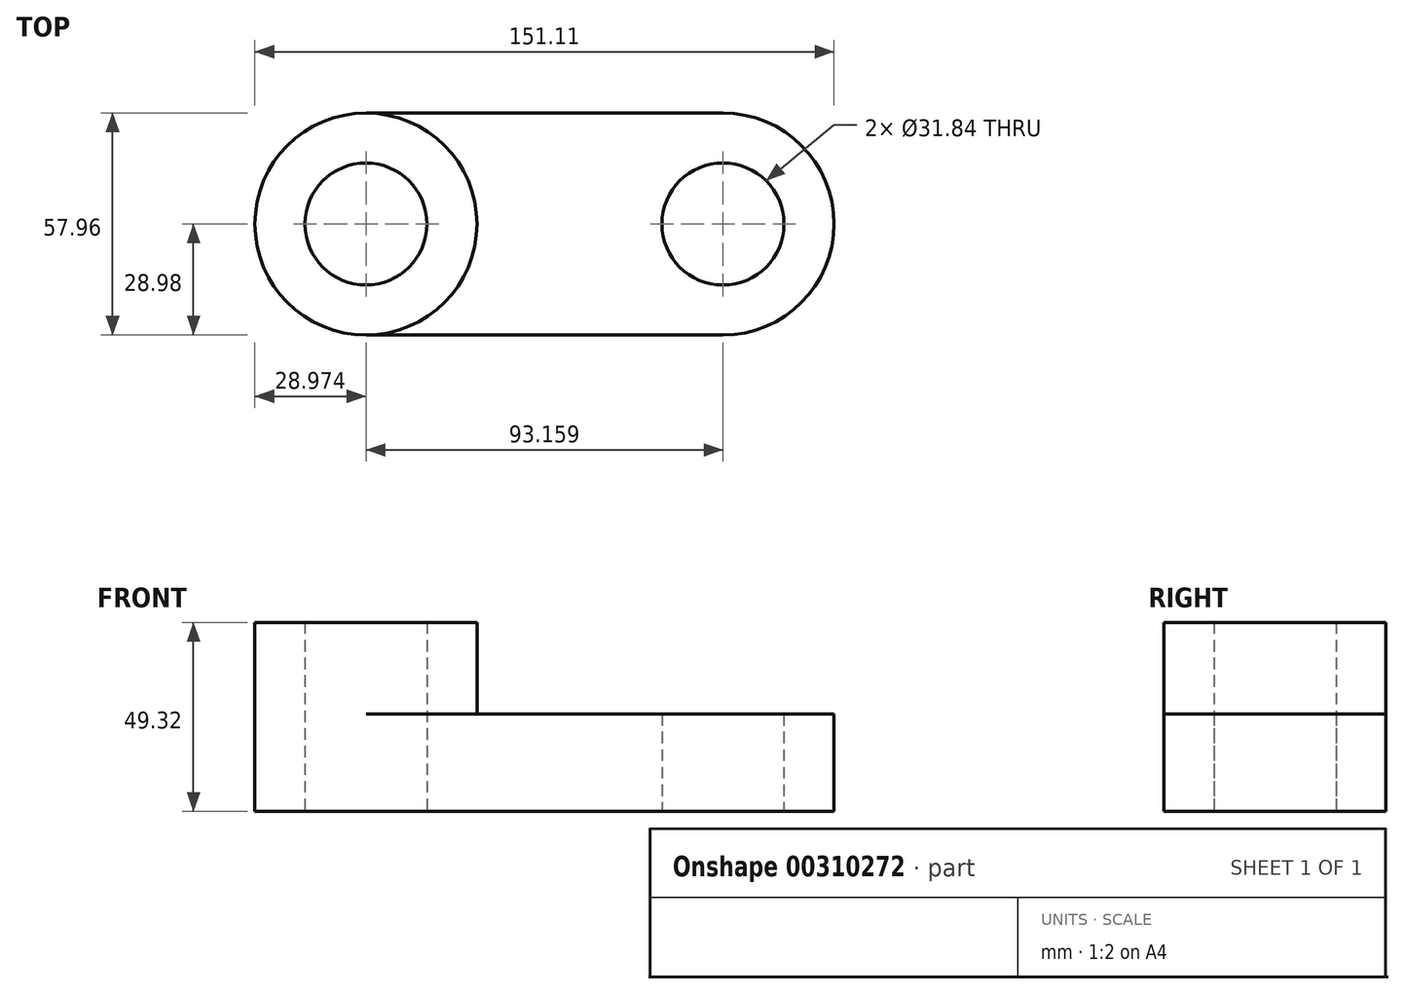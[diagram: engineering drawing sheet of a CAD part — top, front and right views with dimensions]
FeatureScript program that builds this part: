
annotation { "Feature Type Name" : "Feature", "Feature Type Description" : "" }
export const myFeature = defineFeature(function(context is Context, id is Id, definition is map)
    precondition{}
    {
        {
            var Q0;
            Q0=qCreatedBy(makeId("Top.planeOp"),FACE);
            var sketch = newSketch(context, id + "F0", { "sketchPlane" : qUnion([Q0])});
            skLineSegment(sketch, "E0", {"start": v(-142.42, 0) * mm, "end": v(-142.42, 0) * mm});
            skPoint(sketch, "E0.endSnap0", {"position": v(59.82, 0) * mm});
            skLineSegment(sketch, "E1", {"start": v(-49.26, 46.21) * mm, "end": v(-49.26, -63.45) * mm, "construction": true});
            skLineSegment(sketch, "E2", {"start": v(43.9, 44.72) * mm, "end": v(43.9, -62.7) * mm, "construction": true});
            skArc(sketch, "E3", {"start": v(43.9, -28.98) * mm, "mid": v(72.88, 0) * mm, "end": v(43.9, 28.98) * mm});
            skLineSegment(sketch, "E4", {"start": v(-49.26, 28.98) * mm, "end": v(43.9, 28.98) * mm});
            skLineSegment(sketch, "E5", {"start": v(-49.26, -28.98) * mm, "end": v(43.9, -28.98) * mm});
            skPoint(sketch, "E6.orphan", {"position": v(43.9, 15.92) * mm});
            skCircle(sketch, "E7", {"center": v(-49.26, 0) * mm, "radius": 15.92 * mm});
            skCircle(sketch, "E8", {"center": v(43.9, 0) * mm, "radius": 15.92 * mm});
            skLineSegment(sketch, "E9", {"start": v(-96.05, 0) * mm, "end": v(92.92, 0) * mm, "construction": true});
            skPoint(sketch, "E9.endSnap0", {"position": v(72.88, 0) * mm});
            skCircle(sketch, "E10.converted", {"center": v(-49.26, 0) * mm, "radius": 28.98 * mm});
            skSolve(sketch);
        }
        {
            var Q0;
            Q0=makeQuery(id+"F0.imprint","IMPRINT",FACE,{"disambiguationData":[TD([[makeQuery(id+"F0.imprint","IMPRINT",EDGE,{"derivedFrom":sQuery(id+"F0.wireOp",EDGE,"uuXLfyTg-j0G4-Kgvm-Gp7i-tLFSlyMDMfYM")}),1.0]])]});
            var Q1;
            Q1=makeQuery(id+"F0.imprint","IMPRINT",FACE,{"disambiguationData":[TD([[makeQuery(id+"F0.imprint","IMPRINT",EDGE,{"derivedFrom":sQuery(id+"F0.wireOp",EDGE,"E3")}),1.0]])]});
            var Q2;
            Q2=makeQuery(id+"F0.imprint","IMPRINT",FACE,{"disambiguationData":[TD([[makeQuery(id+"F0.imprint","IMPRINT",EDGE,{"derivedFrom":sQuery(id+"F0.wireOp",EDGE,"E7")}),-1.0]])]});
            extrude(context, id + "F1", {"entities" : qUnion([Q0, Q1, Q2]), "depth" : 25.4 * mm});
        }
        {
            var Q0;
            Q0=makeQuery(id+"F0.imprint","IMPRINT",FACE,{"disambiguationData":[TD([[makeQuery(id+"F0.imprint","IMPRINT",EDGE,{"derivedFrom":sQuery(id+"F0.wireOp",EDGE,"E7")}),-1.0]])]});
            extrude(context, id + "F2", {"entities" : qUnion([Q0]), "operationType" : NewBodyOperationType.ADD, "depth" : 49.32 * mm});
        }
    });
